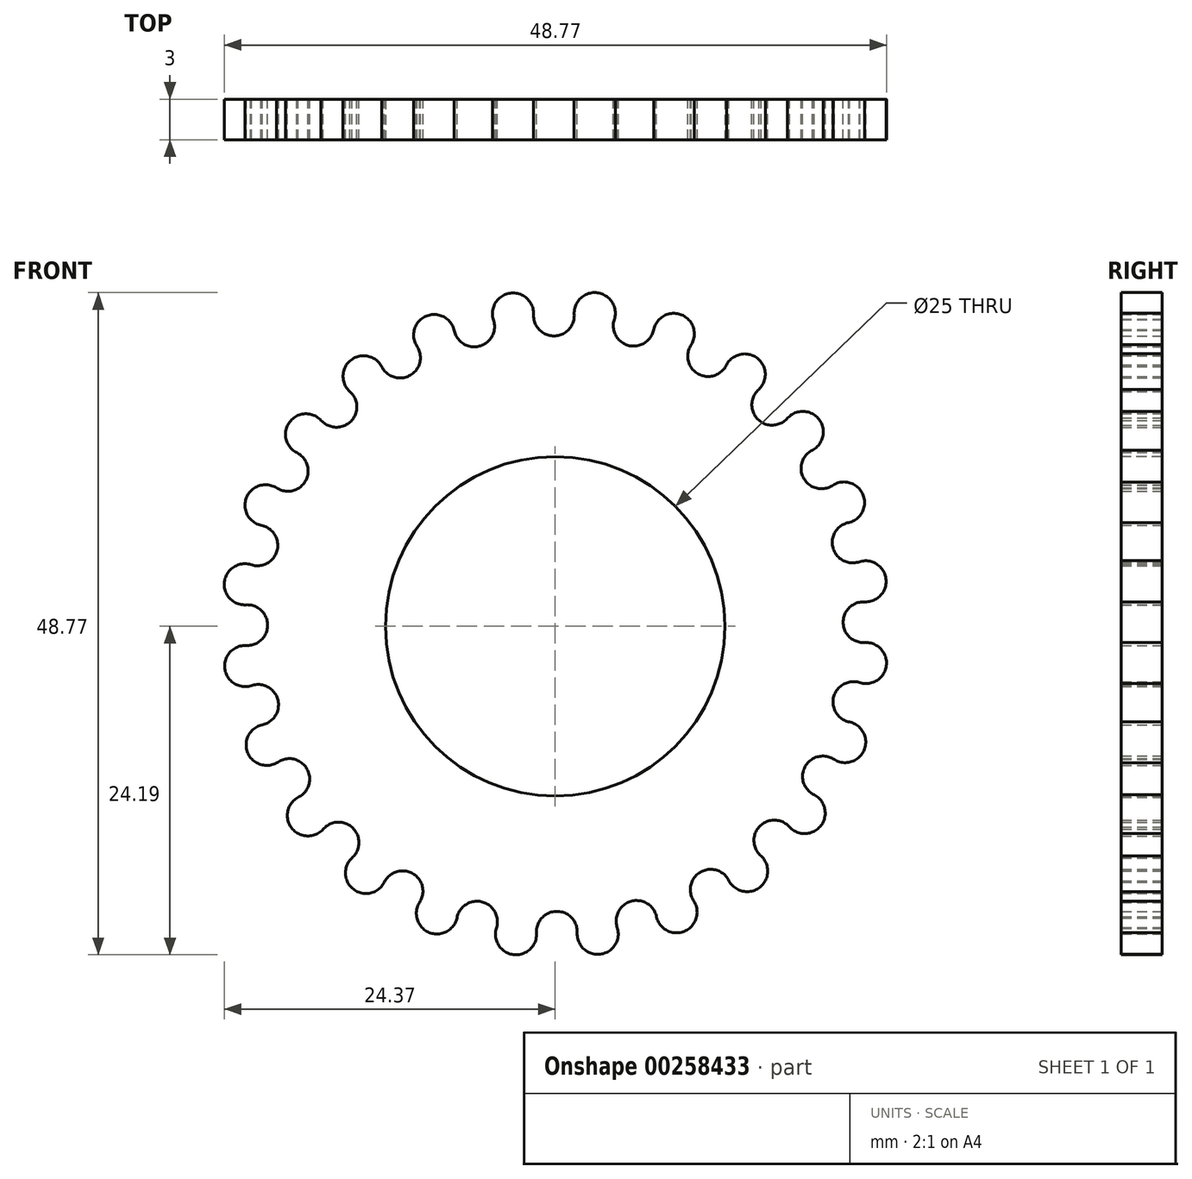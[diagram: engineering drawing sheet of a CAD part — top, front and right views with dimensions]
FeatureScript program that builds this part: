
annotation { "Feature Type Name" : "Feature", "Feature Type Description" : "" }
export const myFeature = defineFeature(function(context is Context, id is Id, definition is map)
    precondition{}
    {
        {
            var Q0;
            Q0=qCreatedBy(makeId("Front.planeOp"),FACE);
            var sketch = newSketch(context, id + "F0", { "sketchPlane" : qUnion([Q0])});
            skArc(sketch, "E0", {"start": v(-1.6, 22.99) * mm, "mid": v(-0.1, 21.39) * mm, "end": v(1.4, 23) * mm});
            skArc(sketch, "E1", {"start": v(4.36, 22.62) * mm, "mid": v(3.1, 24.57) * mm, "end": v(1.4, 23) * mm});
            skArc(sketch, "E2.1.0", {"start": v(-1.6, 22.99) * mm, "mid": v(-3.31, 24.54) * mm, "end": v(-4.55, 22.58) * mm});
            skArc(sketch, "E2.1.1", {"start": v(-7.44, 21.8) * mm, "mid": v(-5.57, 20.64) * mm, "end": v(-4.55, 22.58) * mm});
            skArc(sketch, "E2.2.0", {"start": v(-7.44, 21.8) * mm, "mid": v(-9.5, 22.85) * mm, "end": v(-10.19, 20.64) * mm});
            skArc(sketch, "E2.2.1", {"start": v(-12.77, 19.13) * mm, "mid": v(-10.67, 18.5) * mm, "end": v(-10.19, 20.64) * mm});
            skArc(sketch, "E2.3.0", {"start": v(-12.77, 19.13) * mm, "mid": v(-15.04, 19.62) * mm, "end": v(-15.13, 17.3) * mm});
            skArc(sketch, "E2.3.1", {"start": v(-17.24, 15.18) * mm, "mid": v(-15.04, 15.1) * mm, "end": v(-15.13, 17.3) * mm});
            skArc(sketch, "E2.4.0", {"start": v(-17.24, 15.18) * mm, "mid": v(-19.55, 15.06) * mm, "end": v(-19.04, 12.8) * mm});
            skArc(sketch, "E2.4.1", {"start": v(-20.53, 10.2) * mm, "mid": v(-18.39, 10.7) * mm, "end": v(-19.04, 12.8) * mm});
            skArc(sketch, "E2.5.0", {"start": v(-20.53, 10.2) * mm, "mid": v(-22.73, 9.49) * mm, "end": v(-21.65, 7.44) * mm});
            skArc(sketch, "E2.5.1", {"start": v(-22.42, 4.54) * mm, "mid": v(-20.48, 5.58) * mm, "end": v(-21.65, 7.44) * mm});
            skArc(sketch, "E2.6.0", {"start": v(-22.42, 4.54) * mm, "mid": v(-24.36, 3.29) * mm, "end": v(-22.79, 1.58) * mm});
            skArc(sketch, "E2.6.1", {"start": v(-22.78, -1.4) * mm, "mid": v(-21.18, 0.1) * mm, "end": v(-22.79, 1.58) * mm});
            skArc(sketch, "E2.7.0", {"start": v(-22.78, -1.4) * mm, "mid": v(-24.33, -3.13) * mm, "end": v(-22.37, -4.36) * mm});
            skArc(sketch, "E2.7.1", {"start": v(-21.58, -7.25) * mm, "mid": v(-20.43, -5.39) * mm, "end": v(-22.37, -4.36) * mm});
            skArc(sketch, "E2.8.0", {"start": v(-21.58, -7.25) * mm, "mid": v(-22.64, -9.31) * mm, "end": v(-20.43, -10) * mm});
            skArc(sketch, "E2.8.1", {"start": v(-18.92, -12.59) * mm, "mid": v(-18.29, -10.49) * mm, "end": v(-20.43, -10) * mm});
            skArc(sketch, "E2.9.0", {"start": v(-18.92, -12.59) * mm, "mid": v(-19.4, -14.85) * mm, "end": v(-17.1, -14.95) * mm});
            skArc(sketch, "E2.9.1", {"start": v(-14.97, -17.05) * mm, "mid": v(-14.9, -14.86) * mm, "end": v(-17.1, -14.95) * mm});
            skArc(sketch, "E2.10.0", {"start": v(-14.97, -17.05) * mm, "mid": v(-14.85, -19.37) * mm, "end": v(-12.59, -18.86) * mm});
            skArc(sketch, "E2.10.1", {"start": v(-10, -20.34) * mm, "mid": v(-10.5, -18.2) * mm, "end": v(-12.59, -18.86) * mm});
            skArc(sketch, "E2.11.0", {"start": v(-10, -20.34) * mm, "mid": v(-9.28, -22.54) * mm, "end": v(-7.23, -21.47) * mm});
            skArc(sketch, "E2.11.1", {"start": v(-4.34, -22.23) * mm, "mid": v(-5.37, -20.3) * mm, "end": v(-7.23, -21.47) * mm});
            skArc(sketch, "E2.12.0", {"start": v(-4.34, -22.23) * mm, "mid": v(-3.08, -24.17) * mm, "end": v(-1.37, -22.6) * mm});
            skArc(sketch, "E2.12.1", {"start": v(1.62, -22.6) * mm, "mid": v(0.11, -21) * mm, "end": v(-1.37, -22.6) * mm});
            skArc(sketch, "E2.13.0", {"start": v(1.62, -22.6) * mm, "mid": v(3.34, -24.14) * mm, "end": v(4.57, -22.19) * mm});
            skArc(sketch, "E2.13.1", {"start": v(7.46, -21.4) * mm, "mid": v(5.6, -20.24) * mm, "end": v(4.57, -22.19) * mm});
            skArc(sketch, "E2.14.0", {"start": v(7.46, -21.4) * mm, "mid": v(9.52, -22.45) * mm, "end": v(10.21, -20.24) * mm});
            skArc(sketch, "E2.14.1", {"start": v(12.8, -18.74) * mm, "mid": v(10.7, -18.1) * mm, "end": v(10.21, -20.24) * mm});
            skArc(sketch, "E2.15.0", {"start": v(12.8, -18.74) * mm, "mid": v(15.06, -19.22) * mm, "end": v(15.15, -16.9) * mm});
            skArc(sketch, "E2.15.1", {"start": v(17.26, -14.78) * mm, "mid": v(15.07, -14.71) * mm, "end": v(15.15, -16.9) * mm});
            skArc(sketch, "E2.16.0", {"start": v(17.26, -14.78) * mm, "mid": v(19.57, -14.66) * mm, "end": v(19.06, -12.4) * mm});
            skArc(sketch, "E2.16.1", {"start": v(20.55, -9.8) * mm, "mid": v(18.41, -10.3) * mm, "end": v(19.06, -12.4) * mm});
            skArc(sketch, "E2.17.0", {"start": v(20.55, -9.8) * mm, "mid": v(22.75, -9.1) * mm, "end": v(21.68, -7.04) * mm});
            skArc(sketch, "E2.17.1", {"start": v(22.44, -4.15) * mm, "mid": v(20.5, -5.19) * mm, "end": v(21.68, -7.04) * mm});
            skArc(sketch, "E2.18.0", {"start": v(22.44, -4.15) * mm, "mid": v(24.38, -2.9) * mm, "end": v(22.81, -1.19) * mm});
            skArc(sketch, "E2.18.1", {"start": v(22.8, 1.8) * mm, "mid": v(21.2, 0.3) * mm, "end": v(22.81, -1.19) * mm});
            skArc(sketch, "E2.19.0", {"start": v(22.8, 1.8) * mm, "mid": v(24.35, 3.52) * mm, "end": v(22.4, 4.76) * mm});
            skArc(sketch, "E2.19.1", {"start": v(21.6, 7.65) * mm, "mid": v(20.45, 5.78) * mm, "end": v(22.4, 4.76) * mm});
            skArc(sketch, "E2.20.0", {"start": v(21.6, 7.65) * mm, "mid": v(22.66, 9.7) * mm, "end": v(20.45, 10.4) * mm});
            skArc(sketch, "E2.20.1", {"start": v(18.94, 12.98) * mm, "mid": v(18.31, 10.88) * mm, "end": v(20.45, 10.4) * mm});
            skArc(sketch, "E2.21.0", {"start": v(18.94, 12.98) * mm, "mid": v(19.43, 15.25) * mm, "end": v(17.12, 15.34) * mm});
            skArc(sketch, "E2.21.1", {"start": v(15, 17.45) * mm, "mid": v(14.92, 15.25) * mm, "end": v(17.12, 15.34) * mm});
            skArc(sketch, "E2.22.0", {"start": v(15, 17.45) * mm, "mid": v(14.87, 19.76) * mm, "end": v(12.61, 19.25) * mm});
            skArc(sketch, "E2.22.1", {"start": v(10.02, 20.74) * mm, "mid": v(10.52, 18.6) * mm, "end": v(12.61, 19.25) * mm});
            skArc(sketch, "E2.23.0", {"start": v(10.02, 20.74) * mm, "mid": v(9.3, 22.94) * mm, "end": v(7.25, 21.86) * mm});
            skArc(sketch, "E2.23.1", {"start": v(4.36, 22.62) * mm, "mid": v(5.4, 20.7) * mm, "end": v(7.25, 21.86) * mm});
            skPoint(sketch, "E2.center", {"position": v(0.01, 0.2) * mm});
            skSolve(sketch);
        }
        {
            var Q0;
            Q0=makeQuery(id+"F0.imprint","IMPRINT",FACE,{"disambiguationData":[TD([[makeQuery(id+"F0.imprint","IMPRINT",EDGE,{"derivedFrom":sQuery(id+"F0.wireOp",EDGE,"E0")}),-1.0]])]});
            extrude(context, id + "F1", {"entities" : qUnion([Q0]), "depth" : 3 * mm});
        }
        {
            var Q0;
            Q0=makeQuery(id+"F1.opExtrude","CAP_FACE",FACE,{"disambiguationData":[OSD([sQuery(id+"F0.wireOp",EDGE,"E0"),sQuery(id+"F0.wireOp",EDGE,"E1"),sQuery(id+"F0.wireOp",EDGE,"E2.1.0"),sQuery(id+"F0.wireOp",EDGE,"E2.1.1"),sQuery(id+"F0.wireOp",EDGE,"E2.2.0"),sQuery(id+"F0.wireOp",EDGE,"E2.2.1"),sQuery(id+"F0.wireOp",EDGE,"E2.3.0"),sQuery(id+"F0.wireOp",EDGE,"E2.3.1"),sQuery(id+"F0.wireOp",EDGE,"E2.4.0"),sQuery(id+"F0.wireOp",EDGE,"E2.4.1"),sQuery(id+"F0.wireOp",EDGE,"E2.5.0"),sQuery(id+"F0.wireOp",EDGE,"E2.5.1"),sQuery(id+"F0.wireOp",EDGE,"E2.6.0"),sQuery(id+"F0.wireOp",EDGE,"E2.6.1"),sQuery(id+"F0.wireOp",EDGE,"E2.7.0"),sQuery(id+"F0.wireOp",EDGE,"E2.7.1"),sQuery(id+"F0.wireOp",EDGE,"E2.8.0"),sQuery(id+"F0.wireOp",EDGE,"E2.8.1"),sQuery(id+"F0.wireOp",EDGE,"E2.9.0"),sQuery(id+"F0.wireOp",EDGE,"E2.9.1"),sQuery(id+"F0.wireOp",EDGE,"E2.10.0"),sQuery(id+"F0.wireOp",EDGE,"E2.10.1"),sQuery(id+"F0.wireOp",EDGE,"E2.11.0"),sQuery(id+"F0.wireOp",EDGE,"E2.11.1"),sQuery(id+"F0.wireOp",EDGE,"E2.12.0"),sQuery(id+"F0.wireOp",EDGE,"E2.12.1"),sQuery(id+"F0.wireOp",EDGE,"E2.13.0"),sQuery(id+"F0.wireOp",EDGE,"E2.13.1"),sQuery(id+"F0.wireOp",EDGE,"E2.14.0"),sQuery(id+"F0.wireOp",EDGE,"E2.14.1"),sQuery(id+"F0.wireOp",EDGE,"E2.15.0"),sQuery(id+"F0.wireOp",EDGE,"E2.15.1"),sQuery(id+"F0.wireOp",EDGE,"E2.16.0"),sQuery(id+"F0.wireOp",EDGE,"E2.16.1"),sQuery(id+"F0.wireOp",EDGE,"E2.17.0"),sQuery(id+"F0.wireOp",EDGE,"E2.17.1"),sQuery(id+"F0.wireOp",EDGE,"E2.18.0"),sQuery(id+"F0.wireOp",EDGE,"E2.18.1"),sQuery(id+"F0.wireOp",EDGE,"E2.19.0"),sQuery(id+"F0.wireOp",EDGE,"E2.19.1"),sQuery(id+"F0.wireOp",EDGE,"E2.20.0"),sQuery(id+"F0.wireOp",EDGE,"E2.20.1"),sQuery(id+"F0.wireOp",EDGE,"E2.21.0"),sQuery(id+"F0.wireOp",EDGE,"E2.21.1"),sQuery(id+"F0.wireOp",EDGE,"E2.22.0"),sQuery(id+"F0.wireOp",EDGE,"E2.22.1"),sQuery(id+"F0.wireOp",EDGE,"E2.23.0"),sQuery(id+"F0.wireOp",EDGE,"E2.23.1")])],"isStart":false});
            var sketch = newSketch(context, id + "F2", { "sketchPlane" : qUnion([Q0])});
            skCircle(sketch, "E3", {"center": v(0, 0) * mm, "radius": 12.5 * mm});
            skSolve(sketch);
        }
        {
            var Q0;
            Q0 = qSketchRegion(id + "F2", true);
            extrude(context, id + "F3", {"entities" : qUnion([Q0]), "operationType" : NewBodyOperationType.REMOVE, "oppositeDirection" : true, "depth" : 25 * mm});
        }
    });
